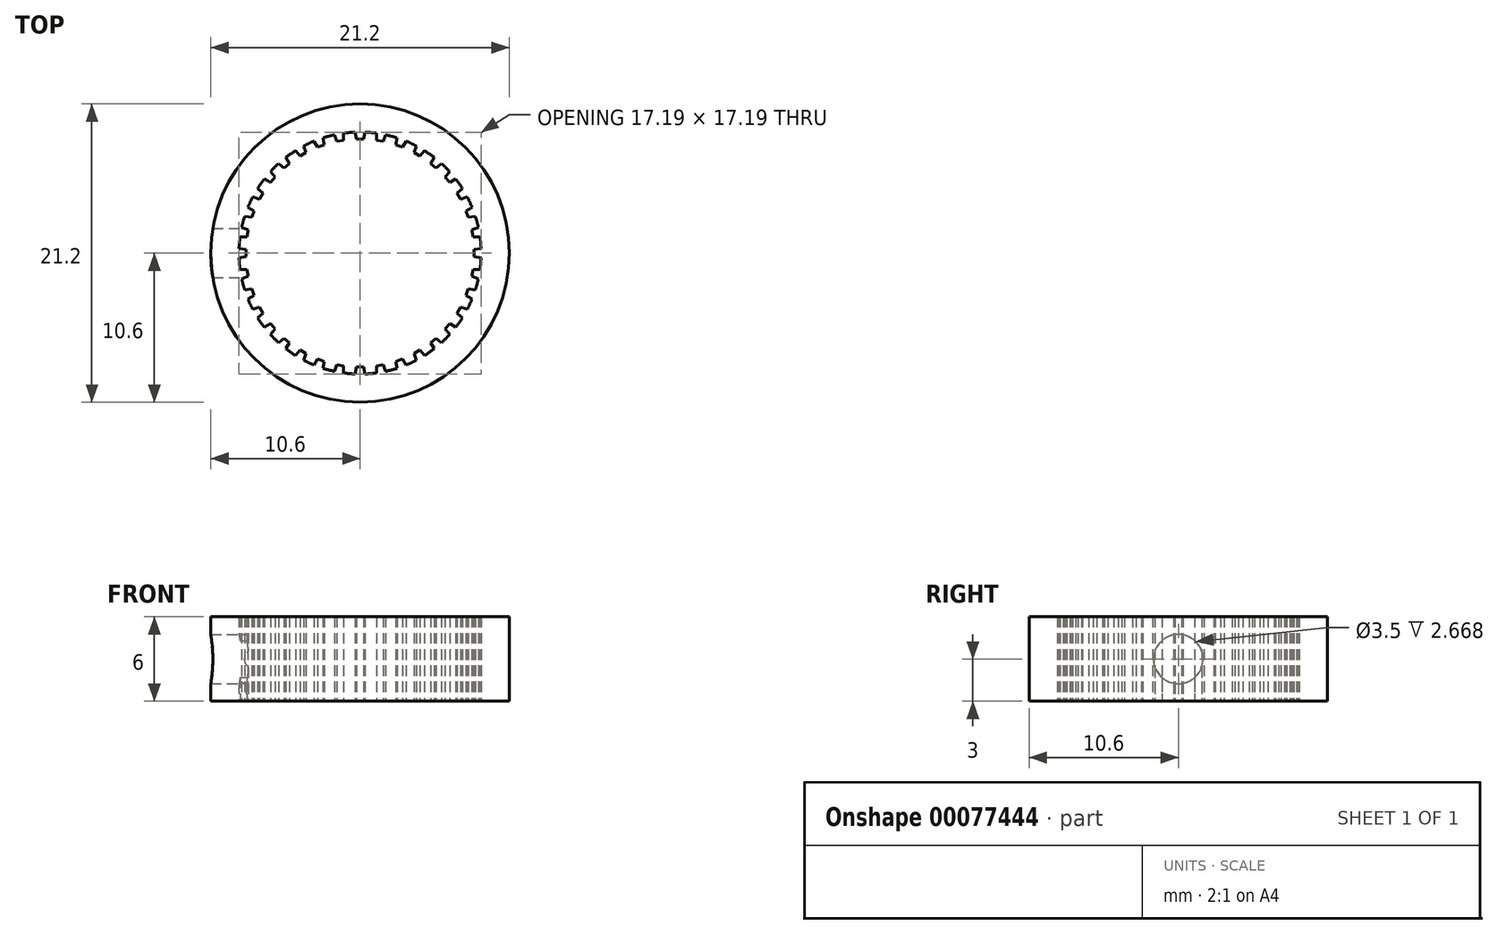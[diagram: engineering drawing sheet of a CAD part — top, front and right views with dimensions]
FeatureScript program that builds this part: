
annotation { "Feature Type Name" : "Feature", "Feature Type Description" : "" }
export const myFeature = defineFeature(function(context is Context, id is Id, definition is map)
    precondition{}
    {
        {
            var Q0;
            Q0=qCreatedBy(makeId("Top.planeOp"),FACE);
            var sketch = newSketch(context, id + "F0", { "sketchPlane" : qUnion([Q0])});
            skCircle(sketch, "E0", {"center": v(0, 0) * mm, "radius": 8.6 * mm});
            skCircle(sketch, "E1", {"center": v(0, 0) * mm, "radius": 10.6 * mm});
            skLineSegment(sketch, "E2", {"start": v(0, 8.6) * mm, "end": v(0, 8.1) * mm, "construction": true});
            skLineSegment(sketch, "E3", {"start": v(-0.25, 8.1) * mm, "end": v(0.25, 8.1) * mm});
            skLineSegment(sketch, "E4", {"start": v(-0.34, 8.6) * mm, "end": v(-0.25, 8.1) * mm});
            skLineSegment(sketch, "E5", {"start": v(0.25, 8.1) * mm, "end": v(0.34, 8.6) * mm});
            skLineSegment(sketch, "E6.1.0", {"start": v(-1.82, 8.4) * mm, "end": v(-1.65, 7.93) * mm});
            skLineSegment(sketch, "E6.1.1", {"start": v(-1.16, 8.02) * mm, "end": v(-1.16, 8.52) * mm});
            skLineSegment(sketch, "E6.1.2", {"start": v(-1.5, 8.47) * mm, "end": v(-1.4, 7.98) * mm, "construction": true});
            skLineSegment(sketch, "E6.1.3", {"start": v(-1.65, 7.93) * mm, "end": v(-1.16, 8.02) * mm});
            skLineSegment(sketch, "E6.2.0", {"start": v(-3.26, 7.96) * mm, "end": v(-3, 7.53) * mm});
            skLineSegment(sketch, "E6.2.1", {"start": v(-2.54, 7.7) * mm, "end": v(-2.62, 8.2) * mm});
            skLineSegment(sketch, "E6.2.2", {"start": v(-2.94, 8.08) * mm, "end": v(-2.77, 7.61) * mm, "construction": true});
            skLineSegment(sketch, "E6.2.3", {"start": v(-3, 7.53) * mm, "end": v(-2.54, 7.7) * mm});
            skLineSegment(sketch, "E7.2.3.0", {"start": v(-4.59, 7.27) * mm, "end": v(-4.27, 6.89) * mm});
            skLineSegment(sketch, "E7.3.3.0", {"start": v(-3.83, 7.14) * mm, "end": v(-4, 7.61) * mm});
            skLineSegment(sketch, "E7.6.3.0", {"start": v(-4.3, 7.45) * mm, "end": v(-4.05, 7.01) * mm, "construction": true});
            skLineSegment(sketch, "E7.9.3.0", {"start": v(-4.27, 6.89) * mm, "end": v(-3.83, 7.14) * mm});
            skLineSegment(sketch, "E7.2.4.0", {"start": v(-5.78, 6.37) * mm, "end": v(-5.4, 6.04) * mm});
            skLineSegment(sketch, "E7.3.4.0", {"start": v(-5.02, 6.37) * mm, "end": v(-5.27, 6.8) * mm});
            skLineSegment(sketch, "E7.6.4.0", {"start": v(-5.53, 6.59) * mm, "end": v(-5.2, 6.2) * mm, "construction": true});
            skLineSegment(sketch, "E7.9.4.0", {"start": v(-5.4, 6.04) * mm, "end": v(-5.02, 6.37) * mm});
            skLineSegment(sketch, "E7.2.5.0", {"start": v(-6.8, 5.27) * mm, "end": v(-6.37, 5.02) * mm});
            skLineSegment(sketch, "E7.3.5.0", {"start": v(-6.04, 5.4) * mm, "end": v(-6.37, 5.78) * mm});
            skLineSegment(sketch, "E7.6.5.0", {"start": v(-6.59, 5.53) * mm, "end": v(-6.2, 5.2) * mm, "construction": true});
            skLineSegment(sketch, "E7.9.5.0", {"start": v(-6.37, 5.02) * mm, "end": v(-6.04, 5.4) * mm});
            skLineSegment(sketch, "E7.2.6.0", {"start": v(-7.61, 4) * mm, "end": v(-7.14, 3.83) * mm});
            skLineSegment(sketch, "E7.3.6.0", {"start": v(-6.89, 4.27) * mm, "end": v(-7.27, 4.59) * mm});
            skLineSegment(sketch, "E7.6.6.0", {"start": v(-7.45, 4.3) * mm, "end": v(-7.01, 4.05) * mm, "construction": true});
            skLineSegment(sketch, "E7.9.6.0", {"start": v(-7.14, 3.83) * mm, "end": v(-6.89, 4.27) * mm});
            skLineSegment(sketch, "E7.2.7.0", {"start": v(-8.2, 2.62) * mm, "end": v(-7.7, 2.54) * mm});
            skLineSegment(sketch, "E7.3.7.0", {"start": v(-7.53, 3) * mm, "end": v(-7.96, 3.26) * mm});
            skLineSegment(sketch, "E7.6.7.0", {"start": v(-8.08, 2.94) * mm, "end": v(-7.61, 2.77) * mm, "construction": true});
            skLineSegment(sketch, "E7.9.7.0", {"start": v(-7.7, 2.54) * mm, "end": v(-7.53, 3) * mm});
            skLineSegment(sketch, "E7.2.8.0", {"start": v(-8.52, 1.16) * mm, "end": v(-8.02, 1.16) * mm});
            skLineSegment(sketch, "E7.3.8.0", {"start": v(-7.93, 1.65) * mm, "end": v(-8.4, 1.82) * mm});
            skLineSegment(sketch, "E7.6.8.0", {"start": v(-8.47, 1.5) * mm, "end": v(-7.98, 1.4) * mm, "construction": true});
            skLineSegment(sketch, "E7.9.8.0", {"start": v(-8.02, 1.16) * mm, "end": v(-7.93, 1.65) * mm});
            skLineSegment(sketch, "E7.2.9.0", {"start": v(-8.6, -0.34) * mm, "end": v(-8.1, -0.25) * mm});
            skLineSegment(sketch, "E7.3.9.0", {"start": v(-8.1, 0.25) * mm, "end": v(-8.6, 0.34) * mm});
            skLineSegment(sketch, "E7.6.9.0", {"start": v(-8.6, 0) * mm, "end": v(-8.1, 0) * mm, "construction": true});
            skLineSegment(sketch, "E7.9.9.0", {"start": v(-8.1, -0.25) * mm, "end": v(-8.1, 0.25) * mm});
            skLineSegment(sketch, "E7.2.10.0", {"start": v(-8.4, -1.82) * mm, "end": v(-7.93, -1.65) * mm});
            skLineSegment(sketch, "E7.3.10.0", {"start": v(-8.02, -1.16) * mm, "end": v(-8.52, -1.16) * mm});
            skLineSegment(sketch, "E7.6.10.0", {"start": v(-8.47, -1.5) * mm, "end": v(-7.98, -1.4) * mm, "construction": true});
            skLineSegment(sketch, "E7.9.10.0", {"start": v(-7.93, -1.65) * mm, "end": v(-8.02, -1.16) * mm});
            skLineSegment(sketch, "E7.2.11.0", {"start": v(-7.96, -3.26) * mm, "end": v(-7.53, -3) * mm});
            skLineSegment(sketch, "E7.3.11.0", {"start": v(-7.7, -2.54) * mm, "end": v(-8.2, -2.62) * mm});
            skLineSegment(sketch, "E7.6.11.0", {"start": v(-8.08, -2.94) * mm, "end": v(-7.61, -2.77) * mm, "construction": true});
            skLineSegment(sketch, "E7.9.11.0", {"start": v(-7.53, -3) * mm, "end": v(-7.7, -2.54) * mm});
            skLineSegment(sketch, "E7.2.12.0", {"start": v(-7.27, -4.59) * mm, "end": v(-6.89, -4.27) * mm});
            skLineSegment(sketch, "E7.3.12.0", {"start": v(-7.14, -3.83) * mm, "end": v(-7.61, -4) * mm});
            skLineSegment(sketch, "E7.6.12.0", {"start": v(-7.45, -4.3) * mm, "end": v(-7.01, -4.05) * mm, "construction": true});
            skLineSegment(sketch, "E7.9.12.0", {"start": v(-6.89, -4.27) * mm, "end": v(-7.14, -3.83) * mm});
            skLineSegment(sketch, "E7.2.13.0", {"start": v(-6.37, -5.78) * mm, "end": v(-6.04, -5.4) * mm});
            skLineSegment(sketch, "E7.3.13.0", {"start": v(-6.37, -5.02) * mm, "end": v(-6.8, -5.27) * mm});
            skLineSegment(sketch, "E7.6.13.0", {"start": v(-6.59, -5.53) * mm, "end": v(-6.2, -5.2) * mm, "construction": true});
            skLineSegment(sketch, "E7.9.13.0", {"start": v(-6.04, -5.4) * mm, "end": v(-6.37, -5.02) * mm});
            skLineSegment(sketch, "E7.2.14.0", {"start": v(-5.27, -6.8) * mm, "end": v(-5.02, -6.37) * mm});
            skLineSegment(sketch, "E7.3.14.0", {"start": v(-5.4, -6.04) * mm, "end": v(-5.78, -6.37) * mm});
            skLineSegment(sketch, "E7.6.14.0", {"start": v(-5.53, -6.59) * mm, "end": v(-5.2, -6.2) * mm, "construction": true});
            skLineSegment(sketch, "E7.9.14.0", {"start": v(-5.02, -6.37) * mm, "end": v(-5.4, -6.04) * mm});
            skLineSegment(sketch, "E7.2.15.0", {"start": v(-4, -7.61) * mm, "end": v(-3.83, -7.14) * mm});
            skLineSegment(sketch, "E7.3.15.0", {"start": v(-4.27, -6.89) * mm, "end": v(-4.59, -7.27) * mm});
            skLineSegment(sketch, "E7.6.15.0", {"start": v(-4.3, -7.45) * mm, "end": v(-4.05, -7.01) * mm, "construction": true});
            skLineSegment(sketch, "E7.9.15.0", {"start": v(-3.83, -7.14) * mm, "end": v(-4.27, -6.89) * mm});
            skLineSegment(sketch, "E7.2.16.0", {"start": v(-2.62, -8.2) * mm, "end": v(-2.54, -7.7) * mm});
            skLineSegment(sketch, "E7.3.16.0", {"start": v(-3, -7.53) * mm, "end": v(-3.26, -7.96) * mm});
            skLineSegment(sketch, "E7.6.16.0", {"start": v(-2.94, -8.08) * mm, "end": v(-2.77, -7.61) * mm, "construction": true});
            skLineSegment(sketch, "E7.9.16.0", {"start": v(-2.54, -7.7) * mm, "end": v(-3, -7.53) * mm});
            skLineSegment(sketch, "E7.2.17.0", {"start": v(-1.16, -8.52) * mm, "end": v(-1.16, -8.02) * mm});
            skLineSegment(sketch, "E7.3.17.0", {"start": v(-1.65, -7.93) * mm, "end": v(-1.82, -8.4) * mm});
            skLineSegment(sketch, "E7.6.17.0", {"start": v(-1.5, -8.47) * mm, "end": v(-1.4, -7.98) * mm, "construction": true});
            skLineSegment(sketch, "E7.9.17.0", {"start": v(-1.16, -8.02) * mm, "end": v(-1.65, -7.93) * mm});
            skLineSegment(sketch, "E7.2.18.0", {"start": v(0.34, -8.6) * mm, "end": v(0.25, -8.1) * mm});
            skLineSegment(sketch, "E7.3.18.0", {"start": v(-0.25, -8.1) * mm, "end": v(-0.34, -8.6) * mm});
            skLineSegment(sketch, "E7.6.18.0", {"start": v(0, -8.6) * mm, "end": v(0, -8.1) * mm, "construction": true});
            skLineSegment(sketch, "E7.9.18.0", {"start": v(0.25, -8.1) * mm, "end": v(-0.25, -8.1) * mm});
            skLineSegment(sketch, "E7.2.19.0", {"start": v(1.82, -8.4) * mm, "end": v(1.65, -7.93) * mm});
            skLineSegment(sketch, "E7.3.19.0", {"start": v(1.16, -8.02) * mm, "end": v(1.16, -8.52) * mm});
            skLineSegment(sketch, "E7.6.19.0", {"start": v(1.5, -8.47) * mm, "end": v(1.4, -7.98) * mm, "construction": true});
            skLineSegment(sketch, "E7.9.19.0", {"start": v(1.65, -7.93) * mm, "end": v(1.16, -8.02) * mm});
            skLineSegment(sketch, "E7.2.20.0", {"start": v(3.26, -7.96) * mm, "end": v(3, -7.53) * mm});
            skLineSegment(sketch, "E7.3.20.0", {"start": v(2.54, -7.7) * mm, "end": v(2.62, -8.2) * mm});
            skLineSegment(sketch, "E7.6.20.0", {"start": v(2.94, -8.08) * mm, "end": v(2.77, -7.61) * mm, "construction": true});
            skLineSegment(sketch, "E7.9.20.0", {"start": v(3, -7.53) * mm, "end": v(2.54, -7.7) * mm});
            skLineSegment(sketch, "E7.2.21.0", {"start": v(4.59, -7.27) * mm, "end": v(4.27, -6.89) * mm});
            skLineSegment(sketch, "E7.3.21.0", {"start": v(3.83, -7.14) * mm, "end": v(4, -7.61) * mm});
            skLineSegment(sketch, "E7.6.21.0", {"start": v(4.3, -7.45) * mm, "end": v(4.05, -7.01) * mm, "construction": true});
            skLineSegment(sketch, "E7.9.21.0", {"start": v(4.27, -6.89) * mm, "end": v(3.83, -7.14) * mm});
            skLineSegment(sketch, "E7.2.22.0", {"start": v(5.78, -6.37) * mm, "end": v(5.4, -6.04) * mm});
            skLineSegment(sketch, "E7.3.22.0", {"start": v(5.02, -6.37) * mm, "end": v(5.27, -6.8) * mm});
            skLineSegment(sketch, "E7.6.22.0", {"start": v(5.53, -6.59) * mm, "end": v(5.2, -6.2) * mm, "construction": true});
            skLineSegment(sketch, "E7.9.22.0", {"start": v(5.4, -6.04) * mm, "end": v(5.02, -6.37) * mm});
            skLineSegment(sketch, "E7.2.23.0", {"start": v(6.8, -5.27) * mm, "end": v(6.37, -5.02) * mm});
            skLineSegment(sketch, "E7.3.23.0", {"start": v(6.04, -5.4) * mm, "end": v(6.37, -5.78) * mm});
            skLineSegment(sketch, "E7.6.23.0", {"start": v(6.59, -5.53) * mm, "end": v(6.2, -5.2) * mm, "construction": true});
            skLineSegment(sketch, "E7.9.23.0", {"start": v(6.37, -5.02) * mm, "end": v(6.04, -5.4) * mm});
            skLineSegment(sketch, "E8.2.24.0", {"start": v(7.61, -4) * mm, "end": v(7.14, -3.83) * mm});
            skLineSegment(sketch, "E8.3.24.0", {"start": v(6.89, -4.27) * mm, "end": v(7.27, -4.59) * mm});
            skLineSegment(sketch, "E8.6.24.0", {"start": v(7.45, -4.3) * mm, "end": v(7.01, -4.05) * mm, "construction": true});
            skLineSegment(sketch, "E8.9.24.0", {"start": v(7.14, -3.83) * mm, "end": v(6.89, -4.27) * mm});
            skLineSegment(sketch, "E8.2.25.0", {"start": v(8.2, -2.62) * mm, "end": v(7.7, -2.54) * mm});
            skLineSegment(sketch, "E8.3.25.0", {"start": v(7.53, -3) * mm, "end": v(7.96, -3.26) * mm});
            skLineSegment(sketch, "E8.6.25.0", {"start": v(8.08, -2.94) * mm, "end": v(7.61, -2.77) * mm, "construction": true});
            skLineSegment(sketch, "E8.9.25.0", {"start": v(7.7, -2.54) * mm, "end": v(7.53, -3) * mm});
            skLineSegment(sketch, "E8.2.26.0", {"start": v(8.52, -1.16) * mm, "end": v(8.02, -1.16) * mm});
            skLineSegment(sketch, "E8.3.26.0", {"start": v(7.93, -1.65) * mm, "end": v(8.4, -1.82) * mm});
            skLineSegment(sketch, "E8.6.26.0", {"start": v(8.47, -1.5) * mm, "end": v(7.98, -1.4) * mm, "construction": true});
            skLineSegment(sketch, "E8.9.26.0", {"start": v(8.02, -1.16) * mm, "end": v(7.93, -1.65) * mm});
            skLineSegment(sketch, "E8.2.27.0", {"start": v(8.6, 0.34) * mm, "end": v(8.1, 0.25) * mm});
            skLineSegment(sketch, "E8.3.27.0", {"start": v(8.1, -0.25) * mm, "end": v(8.6, -0.34) * mm});
            skLineSegment(sketch, "E8.6.27.0", {"start": v(8.6, 0) * mm, "end": v(8.1, 0) * mm, "construction": true});
            skLineSegment(sketch, "E8.9.27.0", {"start": v(8.1, 0.25) * mm, "end": v(8.1, -0.25) * mm});
            skLineSegment(sketch, "E8.2.28.0", {"start": v(8.4, 1.82) * mm, "end": v(7.93, 1.65) * mm});
            skLineSegment(sketch, "E8.3.28.0", {"start": v(8.02, 1.16) * mm, "end": v(8.52, 1.16) * mm});
            skLineSegment(sketch, "E8.6.28.0", {"start": v(8.47, 1.5) * mm, "end": v(7.98, 1.4) * mm, "construction": true});
            skLineSegment(sketch, "E8.9.28.0", {"start": v(7.93, 1.65) * mm, "end": v(8.02, 1.16) * mm});
            skLineSegment(sketch, "E8.2.29.0", {"start": v(7.96, 3.26) * mm, "end": v(7.53, 3) * mm});
            skLineSegment(sketch, "E8.3.29.0", {"start": v(7.7, 2.54) * mm, "end": v(8.2, 2.62) * mm});
            skLineSegment(sketch, "E8.6.29.0", {"start": v(8.08, 2.94) * mm, "end": v(7.61, 2.77) * mm, "construction": true});
            skLineSegment(sketch, "E8.9.29.0", {"start": v(7.53, 3) * mm, "end": v(7.7, 2.54) * mm});
            skLineSegment(sketch, "E9.2.30.0", {"start": v(7.27, 4.59) * mm, "end": v(6.89, 4.27) * mm});
            skLineSegment(sketch, "E9.3.30.0", {"start": v(7.14, 3.83) * mm, "end": v(7.61, 4) * mm});
            skLineSegment(sketch, "E9.6.30.0", {"start": v(7.45, 4.3) * mm, "end": v(7.01, 4.05) * mm, "construction": true});
            skLineSegment(sketch, "E9.9.30.0", {"start": v(6.89, 4.27) * mm, "end": v(7.14, 3.83) * mm});
            skLineSegment(sketch, "E9.2.31.0", {"start": v(6.37, 5.78) * mm, "end": v(6.04, 5.4) * mm});
            skLineSegment(sketch, "E9.3.31.0", {"start": v(6.37, 5.02) * mm, "end": v(6.8, 5.27) * mm});
            skLineSegment(sketch, "E9.6.31.0", {"start": v(6.59, 5.53) * mm, "end": v(6.2, 5.2) * mm, "construction": true});
            skLineSegment(sketch, "E9.9.31.0", {"start": v(6.04, 5.4) * mm, "end": v(6.37, 5.02) * mm});
            skLineSegment(sketch, "E9.2.32.0", {"start": v(5.27, 6.8) * mm, "end": v(5.02, 6.37) * mm});
            skLineSegment(sketch, "E9.3.32.0", {"start": v(5.4, 6.04) * mm, "end": v(5.78, 6.37) * mm});
            skLineSegment(sketch, "E9.6.32.0", {"start": v(5.53, 6.59) * mm, "end": v(5.2, 6.2) * mm, "construction": true});
            skLineSegment(sketch, "E9.9.32.0", {"start": v(5.02, 6.37) * mm, "end": v(5.4, 6.04) * mm});
            skLineSegment(sketch, "E9.2.33.0", {"start": v(4, 7.61) * mm, "end": v(3.83, 7.14) * mm});
            skLineSegment(sketch, "E9.3.33.0", {"start": v(4.27, 6.89) * mm, "end": v(4.59, 7.27) * mm});
            skLineSegment(sketch, "E9.6.33.0", {"start": v(4.3, 7.45) * mm, "end": v(4.05, 7.01) * mm, "construction": true});
            skLineSegment(sketch, "E9.9.33.0", {"start": v(3.83, 7.14) * mm, "end": v(4.27, 6.89) * mm});
            skLineSegment(sketch, "E9.2.34.0", {"start": v(2.62, 8.2) * mm, "end": v(2.54, 7.7) * mm});
            skLineSegment(sketch, "E9.3.34.0", {"start": v(3, 7.53) * mm, "end": v(3.26, 7.96) * mm});
            skLineSegment(sketch, "E9.6.34.0", {"start": v(2.94, 8.08) * mm, "end": v(2.77, 7.61) * mm, "construction": true});
            skLineSegment(sketch, "E9.9.34.0", {"start": v(2.54, 7.7) * mm, "end": v(3, 7.53) * mm});
            skLineSegment(sketch, "E9.2.35.0", {"start": v(1.16, 8.52) * mm, "end": v(1.16, 8.02) * mm});
            skLineSegment(sketch, "E9.3.35.0", {"start": v(1.65, 7.93) * mm, "end": v(1.82, 8.4) * mm});
            skLineSegment(sketch, "E9.6.35.0", {"start": v(1.5, 8.47) * mm, "end": v(1.4, 7.98) * mm, "construction": true});
            skLineSegment(sketch, "E9.9.35.0", {"start": v(1.16, 8.02) * mm, "end": v(1.65, 7.93) * mm});
            skSolve(sketch);
        }
        {
            var Q0;
            Q0=makeQuery(id+"F0.imprint","IMPRINT",FACE,{"disambiguationData":[TD([[makeQuery(id+"F0.imprint","IMPRINT",EDGE,{"derivedFrom":sQuery(id+"F0.wireOp",EDGE,"E1")}),1.0]])]});
            var Q1;
            {var subQ0=sQuery(id+"F0.wireOp",EDGE,"E7.2.3.0");Q1=makeQuery(id+"F0.imprint","IMPRINT",FACE,{"disambiguationData":[TD([[makeQuery(id+"F0.imprint","IMPRINT",EDGE,{"derivedFrom":subQ0}),1.0]])]});}
            var Q2;
            {var subQ0=sQuery(id+"F0.wireOp",EDGE,"E6.2.0");Q2=makeQuery(id+"F0.imprint","IMPRINT",FACE,{"disambiguationData":[TD([[makeQuery(id+"F0.imprint","IMPRINT",EDGE,{"derivedFrom":subQ0}),1.0]])]});}
            var Q3;
            {var subQ0=sQuery(id+"F0.wireOp",EDGE,"E6.1.0");Q3=makeQuery(id+"F0.imprint","IMPRINT",FACE,{"disambiguationData":[TD([[makeQuery(id+"F0.imprint","IMPRINT",EDGE,{"derivedFrom":subQ0}),1.0]])]});}
            var Q4;
            Q4=makeQuery(id+"F0.imprint","IMPRINT",FACE,{"disambiguationData":[TD([[makeQuery(id+"F0.imprint","IMPRINT",EDGE,{"derivedFrom":sQuery(id+"F0.wireOp",EDGE,"E3")}),1.0]])]});
            var Q5;
            {var subQ0=sQuery(id+"F0.wireOp",EDGE,"E9.2.35.0");Q5=makeQuery(id+"F0.imprint","IMPRINT",FACE,{"disambiguationData":[TD([[makeQuery(id+"F0.imprint","IMPRINT",EDGE,{"derivedFrom":subQ0}),1.0]])]});}
            var Q6;
            {var subQ0=sQuery(id+"F0.wireOp",EDGE,"E9.2.34.0");Q6=makeQuery(id+"F0.imprint","IMPRINT",FACE,{"disambiguationData":[TD([[makeQuery(id+"F0.imprint","IMPRINT",EDGE,{"derivedFrom":subQ0}),1.0]])]});}
            var Q7;
            {var subQ0=sQuery(id+"F0.wireOp",EDGE,"E9.2.33.0");Q7=makeQuery(id+"F0.imprint","IMPRINT",FACE,{"disambiguationData":[TD([[makeQuery(id+"F0.imprint","IMPRINT",EDGE,{"derivedFrom":subQ0}),1.0]])]});}
            var Q8;
            {var subQ0=sQuery(id+"F0.wireOp",EDGE,"E9.2.32.0");Q8=makeQuery(id+"F0.imprint","IMPRINT",FACE,{"disambiguationData":[TD([[makeQuery(id+"F0.imprint","IMPRINT",EDGE,{"derivedFrom":subQ0}),1.0]])]});}
            var Q9;
            {var subQ0=sQuery(id+"F0.wireOp",EDGE,"E9.2.31.0");Q9=makeQuery(id+"F0.imprint","IMPRINT",FACE,{"disambiguationData":[TD([[makeQuery(id+"F0.imprint","IMPRINT",EDGE,{"derivedFrom":subQ0}),1.0]])]});}
            var Q10;
            {var subQ0=sQuery(id+"F0.wireOp",EDGE,"E9.2.30.0");Q10=makeQuery(id+"F0.imprint","IMPRINT",FACE,{"disambiguationData":[TD([[makeQuery(id+"F0.imprint","IMPRINT",EDGE,{"derivedFrom":subQ0}),1.0]])]});}
            var Q11;
            {var subQ0=sQuery(id+"F0.wireOp",EDGE,"E8.2.29.0");Q11=makeQuery(id+"F0.imprint","IMPRINT",FACE,{"disambiguationData":[TD([[makeQuery(id+"F0.imprint","IMPRINT",EDGE,{"derivedFrom":subQ0}),1.0]])]});}
            var Q12;
            {var subQ0=sQuery(id+"F0.wireOp",EDGE,"E8.2.28.0");Q12=makeQuery(id+"F0.imprint","IMPRINT",FACE,{"disambiguationData":[TD([[makeQuery(id+"F0.imprint","IMPRINT",EDGE,{"derivedFrom":subQ0}),1.0]])]});}
            var Q13;
            {var subQ0=sQuery(id+"F0.wireOp",EDGE,"E8.2.27.0");Q13=makeQuery(id+"F0.imprint","IMPRINT",FACE,{"disambiguationData":[TD([[makeQuery(id+"F0.imprint","IMPRINT",EDGE,{"derivedFrom":subQ0}),1.0]])]});}
            var Q14;
            {var subQ0=sQuery(id+"F0.wireOp",EDGE,"E8.2.26.0");Q14=makeQuery(id+"F0.imprint","IMPRINT",FACE,{"disambiguationData":[TD([[makeQuery(id+"F0.imprint","IMPRINT",EDGE,{"derivedFrom":subQ0}),1.0]])]});}
            var Q15;
            {var subQ0=sQuery(id+"F0.wireOp",EDGE,"E8.2.25.0");Q15=makeQuery(id+"F0.imprint","IMPRINT",FACE,{"disambiguationData":[TD([[makeQuery(id+"F0.imprint","IMPRINT",EDGE,{"derivedFrom":subQ0}),1.0]])]});}
            var Q16;
            {var subQ0=sQuery(id+"F0.wireOp",EDGE,"E8.2.24.0");Q16=makeQuery(id+"F0.imprint","IMPRINT",FACE,{"disambiguationData":[TD([[makeQuery(id+"F0.imprint","IMPRINT",EDGE,{"derivedFrom":subQ0}),1.0]])]});}
            var Q17;
            {var subQ0=sQuery(id+"F0.wireOp",EDGE,"E7.2.12.0");Q17=makeQuery(id+"F0.imprint","IMPRINT",FACE,{"disambiguationData":[TD([[makeQuery(id+"F0.imprint","IMPRINT",EDGE,{"derivedFrom":subQ0}),1.0]])]});}
            var Q18;
            {var subQ0=sQuery(id+"F0.wireOp",EDGE,"E7.2.11.0");Q18=makeQuery(id+"F0.imprint","IMPRINT",FACE,{"disambiguationData":[TD([[makeQuery(id+"F0.imprint","IMPRINT",EDGE,{"derivedFrom":subQ0}),1.0]])]});}
            var Q19;
            {var subQ0=sQuery(id+"F0.wireOp",EDGE,"E7.2.10.0");Q19=makeQuery(id+"F0.imprint","IMPRINT",FACE,{"disambiguationData":[TD([[makeQuery(id+"F0.imprint","IMPRINT",EDGE,{"derivedFrom":subQ0}),1.0]])]});}
            var Q20;
            {var subQ0=sQuery(id+"F0.wireOp",EDGE,"E7.2.9.0");Q20=makeQuery(id+"F0.imprint","IMPRINT",FACE,{"disambiguationData":[TD([[makeQuery(id+"F0.imprint","IMPRINT",EDGE,{"derivedFrom":subQ0}),1.0]])]});}
            var Q21;
            {var subQ0=sQuery(id+"F0.wireOp",EDGE,"E7.2.8.0");Q21=makeQuery(id+"F0.imprint","IMPRINT",FACE,{"disambiguationData":[TD([[makeQuery(id+"F0.imprint","IMPRINT",EDGE,{"derivedFrom":subQ0}),1.0]])]});}
            var Q22;
            {var subQ0=sQuery(id+"F0.wireOp",EDGE,"E7.2.7.0");Q22=makeQuery(id+"F0.imprint","IMPRINT",FACE,{"disambiguationData":[TD([[makeQuery(id+"F0.imprint","IMPRINT",EDGE,{"derivedFrom":subQ0}),1.0]])]});}
            var Q23;
            {var subQ0=sQuery(id+"F0.wireOp",EDGE,"E7.2.6.0");Q23=makeQuery(id+"F0.imprint","IMPRINT",FACE,{"disambiguationData":[TD([[makeQuery(id+"F0.imprint","IMPRINT",EDGE,{"derivedFrom":subQ0}),1.0]])]});}
            var Q24;
            {var subQ0=sQuery(id+"F0.wireOp",EDGE,"E7.2.5.0");Q24=makeQuery(id+"F0.imprint","IMPRINT",FACE,{"disambiguationData":[TD([[makeQuery(id+"F0.imprint","IMPRINT",EDGE,{"derivedFrom":subQ0}),1.0]])]});}
            var Q25;
            {var subQ0=sQuery(id+"F0.wireOp",EDGE,"E7.2.4.0");Q25=makeQuery(id+"F0.imprint","IMPRINT",FACE,{"disambiguationData":[TD([[makeQuery(id+"F0.imprint","IMPRINT",EDGE,{"derivedFrom":subQ0}),1.0]])]});}
            var Q26;
            {var subQ0=sQuery(id+"F0.wireOp",EDGE,"E7.2.22.0");Q26=makeQuery(id+"F0.imprint","IMPRINT",FACE,{"disambiguationData":[TD([[makeQuery(id+"F0.imprint","IMPRINT",EDGE,{"derivedFrom":subQ0}),1.0]])]});}
            var Q27;
            {var subQ0=sQuery(id+"F0.wireOp",EDGE,"E7.2.21.0");Q27=makeQuery(id+"F0.imprint","IMPRINT",FACE,{"disambiguationData":[TD([[makeQuery(id+"F0.imprint","IMPRINT",EDGE,{"derivedFrom":subQ0}),1.0]])]});}
            var Q28;
            {var subQ0=sQuery(id+"F0.wireOp",EDGE,"E7.2.20.0");Q28=makeQuery(id+"F0.imprint","IMPRINT",FACE,{"disambiguationData":[TD([[makeQuery(id+"F0.imprint","IMPRINT",EDGE,{"derivedFrom":subQ0}),1.0]])]});}
            var Q29;
            {var subQ0=sQuery(id+"F0.wireOp",EDGE,"E7.2.19.0");Q29=makeQuery(id+"F0.imprint","IMPRINT",FACE,{"disambiguationData":[TD([[makeQuery(id+"F0.imprint","IMPRINT",EDGE,{"derivedFrom":subQ0}),1.0]])]});}
            var Q30;
            {var subQ0=sQuery(id+"F0.wireOp",EDGE,"E7.2.18.0");Q30=makeQuery(id+"F0.imprint","IMPRINT",FACE,{"disambiguationData":[TD([[makeQuery(id+"F0.imprint","IMPRINT",EDGE,{"derivedFrom":subQ0}),1.0]])]});}
            var Q31;
            {var subQ0=sQuery(id+"F0.wireOp",EDGE,"E7.2.17.0");Q31=makeQuery(id+"F0.imprint","IMPRINT",FACE,{"disambiguationData":[TD([[makeQuery(id+"F0.imprint","IMPRINT",EDGE,{"derivedFrom":subQ0}),1.0]])]});}
            var Q32;
            {var subQ0=sQuery(id+"F0.wireOp",EDGE,"E7.2.16.0");Q32=makeQuery(id+"F0.imprint","IMPRINT",FACE,{"disambiguationData":[TD([[makeQuery(id+"F0.imprint","IMPRINT",EDGE,{"derivedFrom":subQ0}),1.0]])]});}
            var Q33;
            {var subQ0=sQuery(id+"F0.wireOp",EDGE,"E7.2.15.0");Q33=makeQuery(id+"F0.imprint","IMPRINT",FACE,{"disambiguationData":[TD([[makeQuery(id+"F0.imprint","IMPRINT",EDGE,{"derivedFrom":subQ0}),1.0]])]});}
            var Q34;
            {var subQ0=sQuery(id+"F0.wireOp",EDGE,"E7.2.14.0");Q34=makeQuery(id+"F0.imprint","IMPRINT",FACE,{"disambiguationData":[TD([[makeQuery(id+"F0.imprint","IMPRINT",EDGE,{"derivedFrom":subQ0}),1.0]])]});}
            var Q35;
            {var subQ0=sQuery(id+"F0.wireOp",EDGE,"E7.2.13.0");Q35=makeQuery(id+"F0.imprint","IMPRINT",FACE,{"disambiguationData":[TD([[makeQuery(id+"F0.imprint","IMPRINT",EDGE,{"derivedFrom":subQ0}),1.0]])]});}
            var Q36;
            {var subQ0=sQuery(id+"F0.wireOp",EDGE,"E7.2.23.0");Q36=makeQuery(id+"F0.imprint","IMPRINT",FACE,{"disambiguationData":[TD([[makeQuery(id+"F0.imprint","IMPRINT",EDGE,{"derivedFrom":subQ0}),1.0]])]});}
            extrude(context, id + "F1", {"entities" : qUnion([Q0, Q1, Q2, Q3, Q4, Q5, Q6, Q7, Q8, Q9, Q10, Q11, Q12, Q13, Q14, Q15, Q16, Q17, Q18, Q19, Q20, Q21, Q22, Q23, Q24, Q25, Q26, Q27, Q28, Q29, Q30, Q31, Q32, Q33, Q34, Q35, Q36]), "depth" : 6 * mm});
        }
        {
            var Q0;
            Q0=qCreatedBy(makeId("Right.planeOp"),FACE);
            var sketch = newSketch(context, id + "F2", { "sketchPlane" : qUnion([Q0])});
            skLineSegment(sketch, "E10", {"start": v(0, 0) * mm, "end": v(0, 3) * mm});
            skCircle(sketch, "E11", {"center": v(0, 3) * mm, "radius": 1.75 * mm});
            skSolve(sketch);
        }
        {
            var Q0;
            Q0=qSketchRegion(id+"F2",true);
            extrude(context, id + "F3", {"entities" : qUnion([Q0]), "operationType" : NewBodyOperationType.REMOVE, "oppositeDirection" : true, "depth" : 25 * mm});
        }
    });
